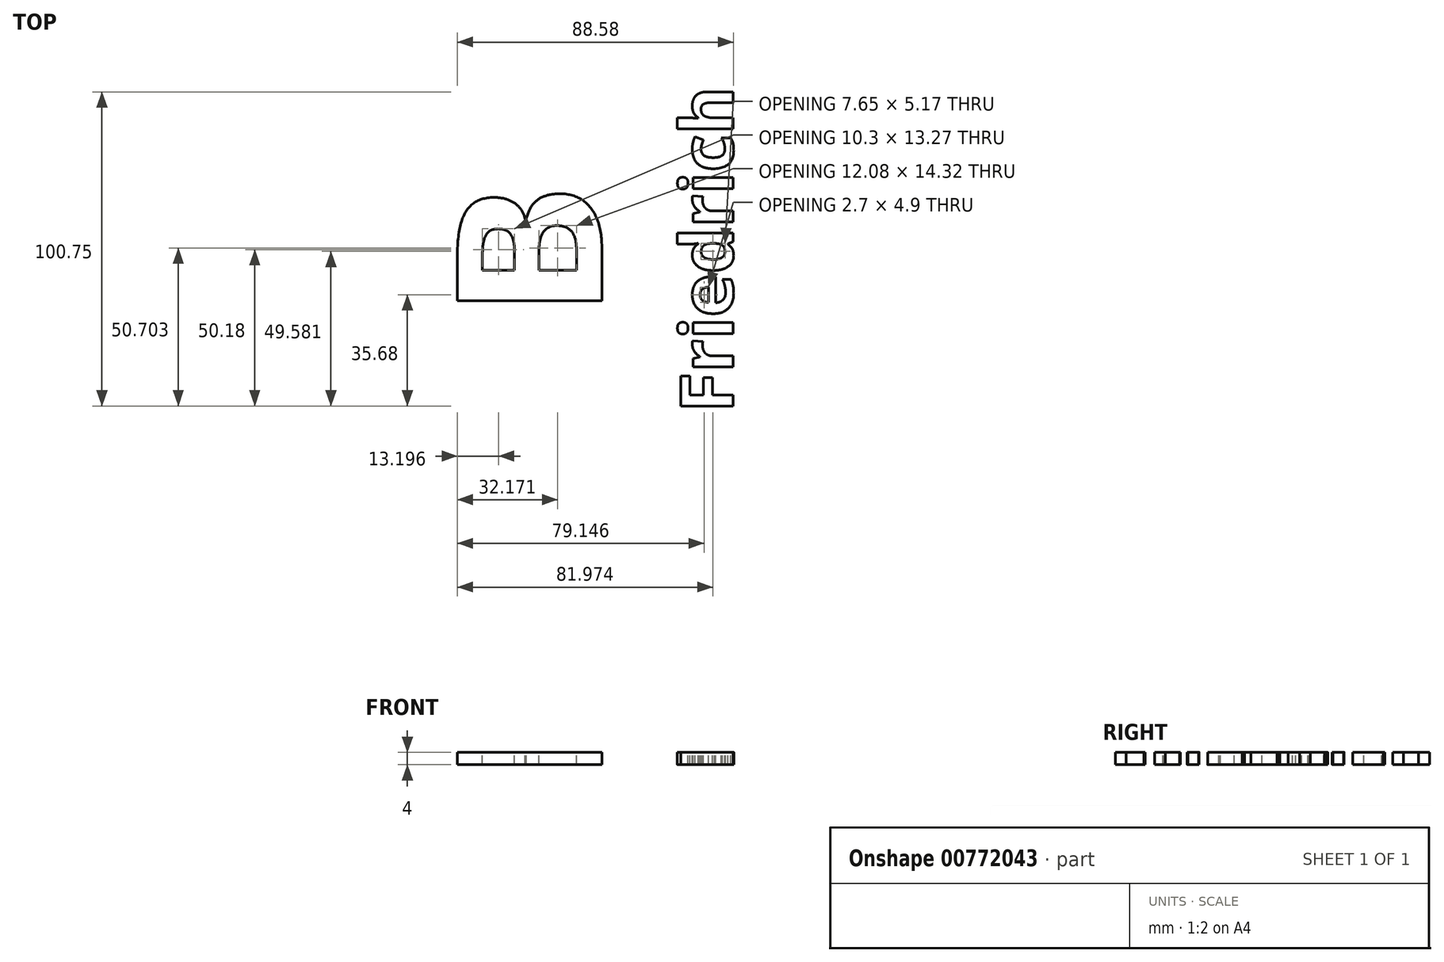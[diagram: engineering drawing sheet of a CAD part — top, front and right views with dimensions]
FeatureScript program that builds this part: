
annotation { "Feature Type Name" : "Feature", "Feature Type Description" : "" }
export const myFeature = defineFeature(function(context is Context, id is Id, definition is map)
    precondition{}
    {
        {
            var Q0;
            Q0=qCreatedBy(makeId("Top.planeOp"),FACE);
            var sketch = newSketch(context, id + "F0", { "sketchPlane" : qUnion([Q0])});
            skText(sketch, "E0", { "text": "B", "fontName": "OpenSans-Bold.ttf"});
            skText(sketch, "E1", { "text": "Friedrich", "fontName": "OpenSans-Bold.ttf"});
            const initialGuessF0  = {"E0": [0, -0.0222, 0, 1, 0.04672], "E1": [0.04203, -0.0522, 0, 1, 0.01688]};
            skSetInitialGuess(sketch, initialGuessF0);
            skSolve(sketch);
        }
        {
            var Q0;
            Q0 = qSketchRegion(id + "F0", true);
            extrude(context, id + "F1", {"entities" : qUnion([Q0]), "oppositeDirection" : true, "depth" : 4 * mm, "offsetDistance" : 25 * mm});
        }
    });
